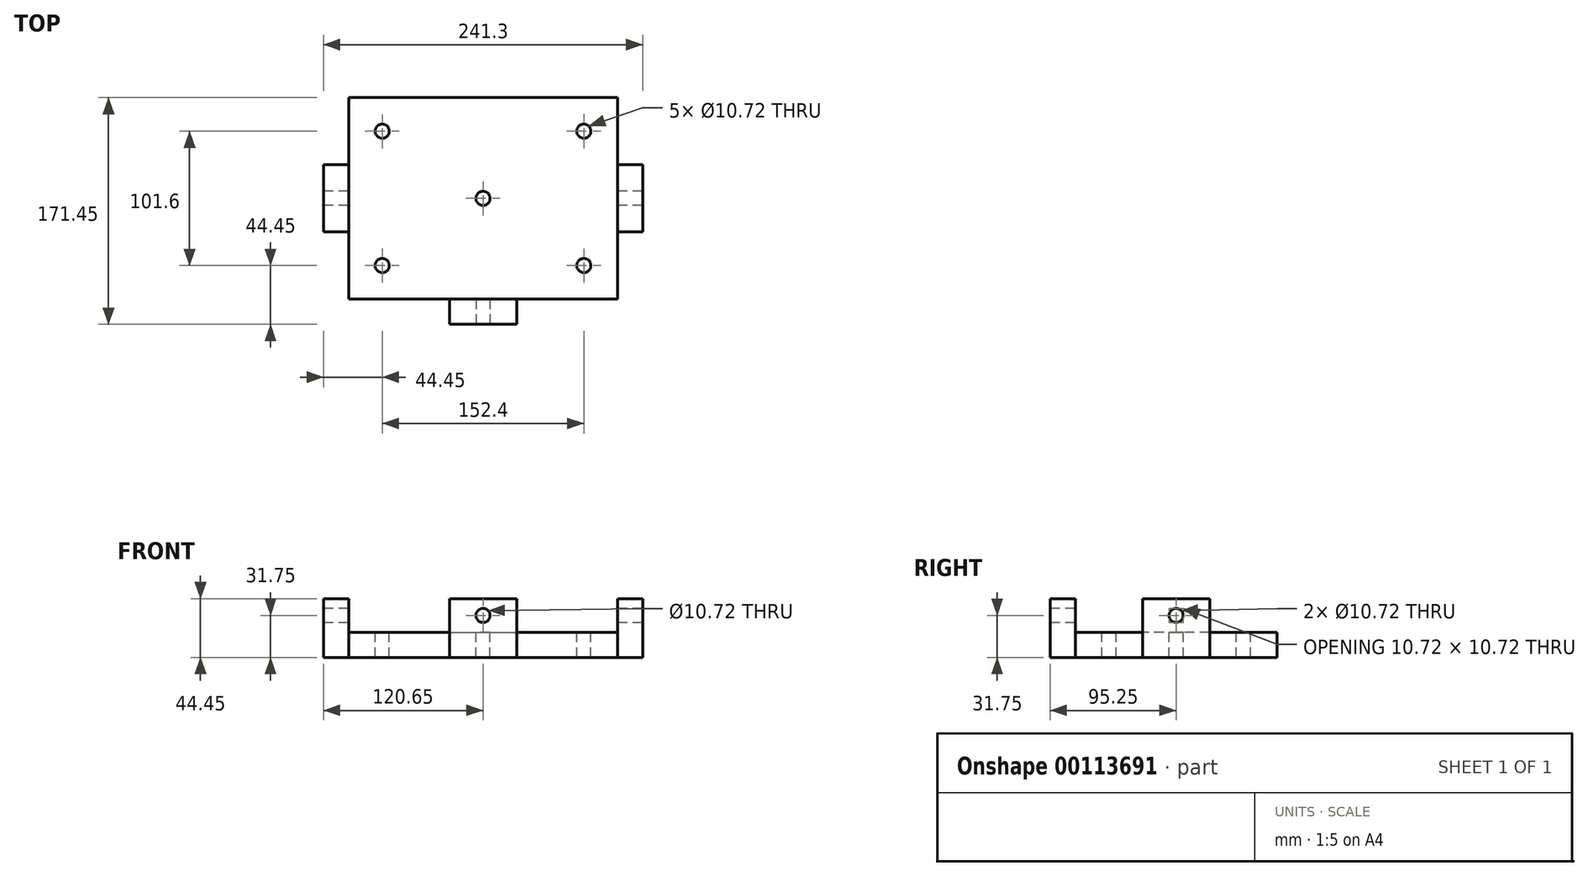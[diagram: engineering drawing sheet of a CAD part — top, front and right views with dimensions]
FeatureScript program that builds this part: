
annotation { "Feature Type Name" : "Feature", "Feature Type Description" : "" }
export const myFeature = defineFeature(function(context is Context, id is Id, definition is map)
    precondition{}
    {
        {
            var Q0;
            Q0=qCreatedBy(makeId("Top.planeOp"),FACE);
            var sketch = newSketch(context, id + "F0", { "sketchPlane" : qUnion([Q0])});
            skLineSegment(sketch, "E0.bottom", {"start": v(-101.6, 76.2) * mm, "end": v(101.6, 76.2) * mm});
            skLineSegment(sketch, "E0.top", {"start": v(-101.6, -76.2) * mm, "end": v(101.6, -76.2) * mm});
            skLineSegment(sketch, "E0.left", {"start": v(-101.6, 76.2) * mm, "end": v(-101.6, -76.2) * mm});
            skLineSegment(sketch, "E0.right", {"start": v(101.6, 76.2) * mm, "end": v(101.6, -76.2) * mm});
            skPoint(sketch, "E0.middle", {"position": v(0, 0) * mm});
            skLineSegment(sketch, "E1.bottom", {"start": v(-76.2, 50.8) * mm, "end": v(76.2, 50.8) * mm, "construction": true});
            skLineSegment(sketch, "E1.top", {"start": v(-76.2, -50.8) * mm, "end": v(76.2, -50.8) * mm, "construction": true});
            skLineSegment(sketch, "E1.left", {"start": v(-76.2, 50.8) * mm, "end": v(-76.2, -50.8) * mm, "construction": true});
            skLineSegment(sketch, "E1.right", {"start": v(76.2, 50.8) * mm, "end": v(76.2, -50.8) * mm, "construction": true});
            skSolve(sketch);
        }
        {
            var Q0;
            Q0 = qSketchRegion(id + "F0", true);
            extrude(context, id + "F1", {"entities" : qUnion([Q0]), "depth" : 19.05 * mm});
        }
        {
            var Q0;
            Q0=makeQuery(id+"F1.opExtrude","CAP_FACE",FACE,{"disambiguationData":[OSD([sQuery(id+"F0.wireOp",EDGE,"E0.bottom"),sQuery(id+"F0.wireOp",EDGE,"E0.top"),sQuery(id+"F0.wireOp",EDGE,"E0.left"),sQuery(id+"F0.wireOp",EDGE,"E0.right")])],"isStart":false});
            var sketch = newSketch(context, id + "F2", { "sketchPlane" : qUnion([Q0])});
            skLineSegment(sketch, "E2.0", {"start": v(-76.2, 50.8) * mm, "end": v(76.2, 50.8) * mm, "construction": true});
            skLineSegment(sketch, "E3.0", {"start": v(-76.2, 50.8) * mm, "end": v(-76.2, -50.8) * mm, "construction": true});
            skLineSegment(sketch, "E4.0", {"start": v(-76.2, -50.8) * mm, "end": v(76.2, -50.8) * mm, "construction": true});
            skLineSegment(sketch, "E5.0", {"start": v(76.2, 50.8) * mm, "end": v(76.2, -50.8) * mm, "construction": true});
            skPoint(sketch, "E6", {"position": v(0, 0) * mm});
            skPoint(sketch, "E7", {"position": v(-76.2, 50.8) * mm});
            skPoint(sketch, "E8", {"position": v(76.2, 50.8) * mm});
            skPoint(sketch, "E9", {"position": v(76.2, -50.8) * mm});
            skPoint(sketch, "E10", {"position": v(-76.2, -50.8) * mm});
            skSolve(sketch);
        }
        {
            var Q0;
            Q0=sQuery(id+"F2.wireOp",VERTEX,"E7");
            var Q1;
            Q1=sQuery(id+"F2.wireOp",VERTEX,"E8");
            var Q2;
            Q2=sQuery(id+"F2.wireOp",VERTEX,"E6");
            var Q3;
            Q3=sQuery(id+"F2.wireOp",VERTEX,"E10");
            var Q4;
            Q4=sQuery(id+"F2.wireOp",VERTEX,"E9");
            var Q5;
            Q5=makeQuery(id+"F1.opExtrude","SWEPT_BODY",BODY,{"disambiguationData":[OSD([sQuery(id+"F0.wireOp",EDGE,"E0.bottom"),sQuery(id+"F0.wireOp",EDGE,"E0.top"),sQuery(id+"F0.wireOp",EDGE,"E0.left"),sQuery(id+"F0.wireOp",EDGE,"E0.right")])]});
            hole(context, id + "F3", {"style" : HoleStyle.SIMPLE, "endStyle" : HoleEndStyle.THROUGH, "standardTappedOrClearance" : lookupTablePath({ "standard" : "ANSI", "engagement" : "75%", "pitch" : "13 tpi", "size" : "1/2", "type" : "Tapped" }), "standardBlindInLast" : lookupTablePath({ "standard" : "ANSI", "engagement" : "75%", "pitch" : "13 tpi", "size" : "1/2", "type" : "Tapped" }), "holeDiameter" : 10.72 * mm, "locations" : qUnion([Q0, Q1, Q2, Q3, Q4]), "scope" : qUnion([Q5]), "isTappedThrough" : true, "majorDiameter" : 12.7 * mm, "showTappedDepth" : true});
        }
        {
            var Q0;
            Q0=makeQuery(id+"F0.imprint","IMPRINT",FACE,{"disambiguationData":[TD([[makeQuery(id+"F0.imprint","IMPRINT",EDGE,{"derivedFrom":sQuery(id+"F0.wireOp",EDGE,"E0.bottom")}),-1.0]])]});
            var sketch = newSketch(context, id + "F4", { "sketchPlane" : qUnion([Q0])});
            skLineSegment(sketch, "E11", {"start": v(-141.75, 0) * mm, "end": v(128.24, 0) * mm, "construction": true});
            skLineSegment(sketch, "E12", {"start": v(0, -93.67) * mm, "end": v(0, 85.34) * mm, "construction": true});
            skLineSegment(sketch, "E13.0", {"start": v(-141.75, -25.4) * mm, "end": v(128.24, -25.4) * mm, "construction": true});
            skLineSegment(sketch, "E14.0", {"start": v(-25.4, -93.67) * mm, "end": v(-25.4, 85.34) * mm, "construction": true});
            skLineSegment(sketch, "E15.0", {"start": v(-101.6, 76.2) * mm, "end": v(-101.6, -76.2) * mm, "construction": true});
            skLineSegment(sketch, "E16.0", {"start": v(-101.6, -76.2) * mm, "end": v(101.6, -76.2) * mm, "construction": true});
            skLineSegment(sketch, "E17.bottom", {"start": v(-101.6, -25.4) * mm, "end": v(-120.65, -25.4) * mm});
            skLineSegment(sketch, "E17.top", {"start": v(-101.6, 25.4) * mm, "end": v(-120.65, 25.4) * mm});
            skLineSegment(sketch, "E17.left", {"start": v(-101.6, -25.4) * mm, "end": v(-101.6, 25.4) * mm});
            skLineSegment(sketch, "E17.right", {"start": v(-120.65, -25.4) * mm, "end": v(-120.65, 25.4) * mm});
            skLineSegment(sketch, "E18.bottom", {"start": v(-25.4, -76.2) * mm, "end": v(25.4, -76.2) * mm});
            skLineSegment(sketch, "E18.top", {"start": v(-25.4, -95.25) * mm, "end": v(25.4, -95.25) * mm});
            skLineSegment(sketch, "E18.left", {"start": v(-25.4, -76.2) * mm, "end": v(-25.4, -95.25) * mm});
            skLineSegment(sketch, "E18.right", {"start": v(25.4, -76.2) * mm, "end": v(25.4, -95.25) * mm});
            skLineSegment(sketch, "E19.MirrorCS", {"start": v(101.6, -25.4) * mm, "end": v(120.65, -25.4) * mm});
            skLineSegment(sketch, "E20.MirrorCS", {"start": v(101.6, 25.4) * mm, "end": v(120.65, 25.4) * mm});
            skLineSegment(sketch, "E21.MirrorCS", {"start": v(120.65, -25.4) * mm, "end": v(120.65, 25.4) * mm});
            skLineSegment(sketch, "E22.MirrorCS", {"start": v(101.6, -25.4) * mm, "end": v(101.6, 25.4) * mm});
            skSolve(sketch);
        }
        {
            var Q0;
            Q0 = qSketchRegion(id + "F4", true);
            extrude(context, id + "F5", {"entities" : qUnion([Q0]), "operationType" : NewBodyOperationType.ADD, "depth" : 44.45 * mm});
        }
        {
            var Q0;
            Q0=makeQuery(id+"F5.opExtrude","SWEPT_FACE",FACE,{"disambiguationData":[OSD([sQuery(id+"F4.wireOp",EDGE,"E18.top")])]});
            var sketch = newSketch(context, id + "F6", { "sketchPlane" : qUnion([Q0])});
            skLineSegment(sketch, "E23.0", {"start": v(-25.4, 0) * mm, "end": v(25.4, 0) * mm, "construction": true});
            skLineSegment(sketch, "E24.0", {"start": v(-25.4, 31.75) * mm, "end": v(25.4, 31.75) * mm, "construction": true});
            skPoint(sketch, "E25", {"position": v(0, 31.75) * mm});
            skSolve(sketch);
        }
        {
            var Q0;
            Q0=sQuery(id+"F6.wireOp",VERTEX,"E25");
            var Q1;
            Q1=makeQuery(id+"F1.opExtrude","SWEPT_BODY",BODY,{"disambiguationData":[OSD([sQuery(id+"F0.wireOp",EDGE,"E0.bottom"),sQuery(id+"F0.wireOp",EDGE,"E0.top"),sQuery(id+"F0.wireOp",EDGE,"E0.left"),sQuery(id+"F0.wireOp",EDGE,"E0.right")])]});
            hole(context, id + "F7", {"style" : HoleStyle.SIMPLE, "endStyle" : HoleEndStyle.THROUGH, "standardTappedOrClearance" : lookupTablePath({ "standard" : "ANSI", "engagement" : "75%", "pitch" : "13 tpi", "size" : "1/2", "type" : "Tapped" }), "standardBlindInLast" : lookupTablePath({ "standard" : "ANSI", "engagement" : "75%", "pitch" : "13 tpi", "size" : "1/2", "type" : "Tapped" }), "holeDiameter" : 10.72 * mm, "locations" : qUnion([Q0]), "scope" : qUnion([Q1]), "isTappedThrough" : true, "majorDiameter" : 12.7 * mm, "showTappedDepth" : true});
        }
        {
            var Q0;
            Q0=makeQuery(id+"F5.opExtrude","SWEPT_FACE",FACE,{"disambiguationData":[OSD([sQuery(id+"F4.wireOp",EDGE,"E17.right")])]});
            var sketch = newSketch(context, id + "F8", { "sketchPlane" : qUnion([Q0])});
            skLineSegment(sketch, "E26.0", {"start": v(25.4, 0) * mm, "end": v(-25.4, 0) * mm, "construction": true});
            skLineSegment(sketch, "E27.0", {"start": v(25.4, 31.75) * mm, "end": v(-25.4, 31.75) * mm, "construction": true});
            skPoint(sketch, "E28", {"position": v(0, 31.75) * mm});
            skSolve(sketch);
        }
        {
            var Q0;
            Q0=sQuery(id+"F8.wireOp",VERTEX,"E28");
            var Q1;
            Q1=makeQuery(id+"F1.opExtrude","SWEPT_BODY",BODY,{"disambiguationData":[OSD([sQuery(id+"F0.wireOp",EDGE,"E0.bottom"),sQuery(id+"F0.wireOp",EDGE,"E0.top"),sQuery(id+"F0.wireOp",EDGE,"E0.left"),sQuery(id+"F0.wireOp",EDGE,"E0.right")])]});
            hole(context, id + "F9", {"style" : HoleStyle.SIMPLE, "endStyle" : HoleEndStyle.THROUGH, "standardTappedOrClearance" : lookupTablePath({ "standard" : "ANSI", "engagement" : "75%", "pitch" : "13 tpi", "size" : "1/2", "type" : "Tapped" }), "standardBlindInLast" : lookupTablePath({ "standard" : "ANSI", "engagement" : "75%", "pitch" : "13 tpi", "size" : "1/2", "type" : "Tapped" }), "holeDiameter" : 10.72 * mm, "locations" : qUnion([Q0]), "scope" : qUnion([Q1]), "isTappedThrough" : true, "majorDiameter" : 12.7 * mm, "showTappedDepth" : true});
        }
    });
